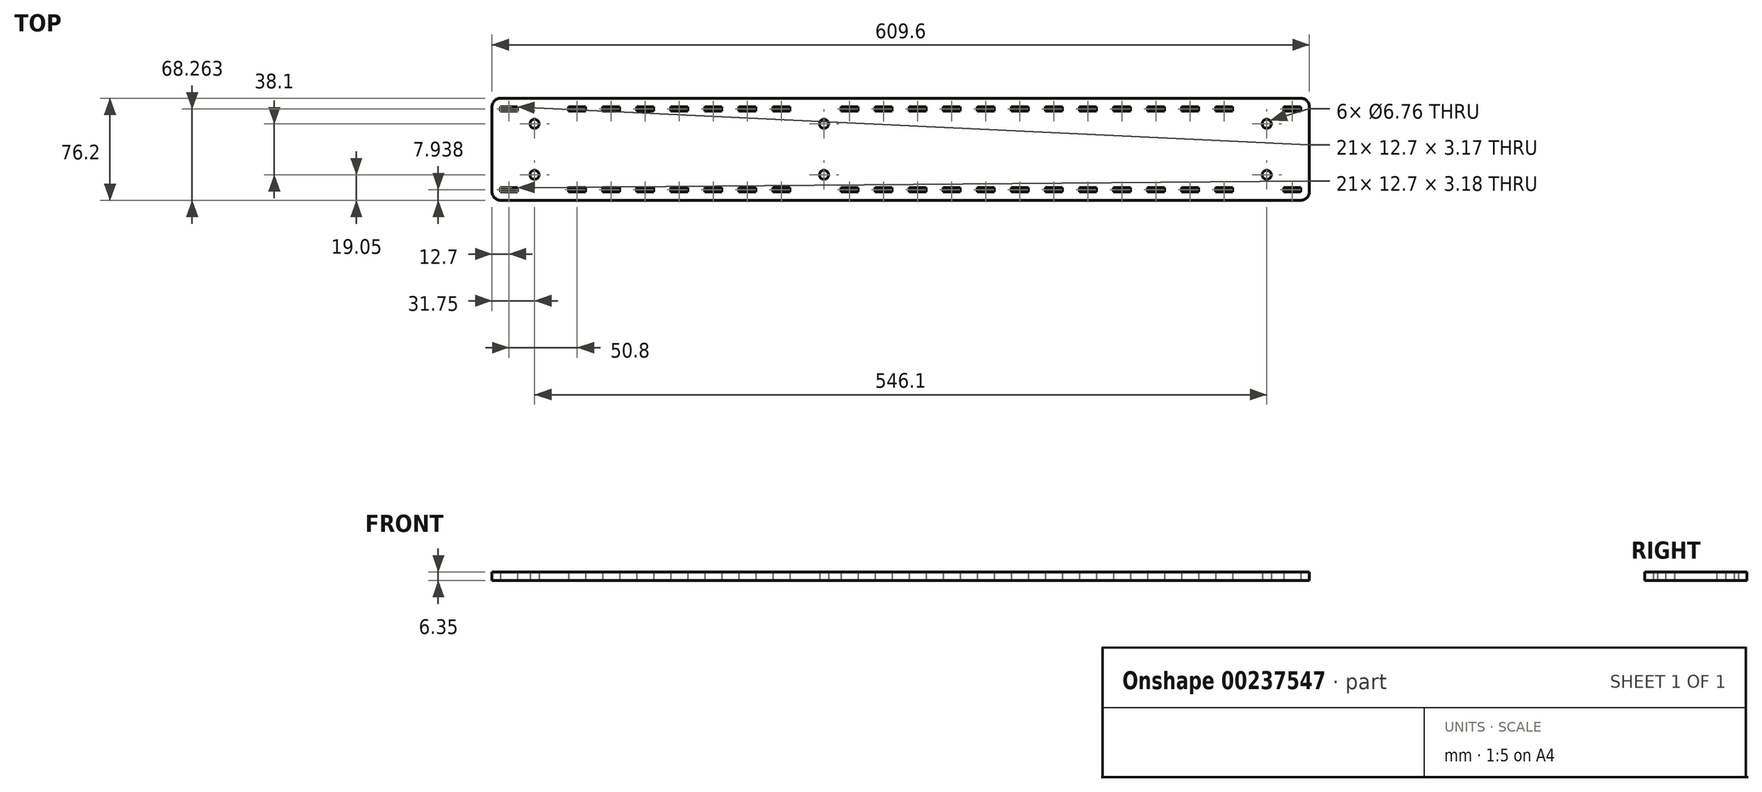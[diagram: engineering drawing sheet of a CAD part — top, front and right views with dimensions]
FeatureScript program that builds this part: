
annotation { "Feature Type Name" : "Feature", "Feature Type Description" : "" }
export const myFeature = defineFeature(function(context is Context, id is Id, definition is map)
    precondition{}
    {
        {
            var Q0;
            Q0=qCreatedBy(makeId("Top.planeOp"),FACE);
            var sketch = newSketch(context, id + "F0", { "sketchPlane" : qUnion([Q0])});
            skLineSegment(sketch, "E0.bottom", {"start": v(0, 0) * mm, "end": v(609.6, 0) * mm});
            skLineSegment(sketch, "E0.top", {"start": v(0, 76.2) * mm, "end": v(609.6, 76.2) * mm});
            skLineSegment(sketch, "E0.left", {"start": v(0, 0) * mm, "end": v(0, 76.2) * mm});
            skLineSegment(sketch, "E0.right", {"start": v(609.6, 0) * mm, "end": v(609.6, 76.2) * mm});
            skLineSegment(sketch, "E1", {"start": v(0, 76.2) * mm, "end": v(0, 69.85) * mm});
            skLineSegment(sketch, "E2", {"start": v(6.35, 69.85) * mm, "end": v(6.35, 66.68) * mm});
            skLineSegment(sketch, "E3", {"start": v(6.35, 66.68) * mm, "end": v(19.05, 66.68) * mm});
            skLineSegment(sketch, "E4", {"start": v(19.05, 66.68) * mm, "end": v(19.05, 69.85) * mm});
            skLineSegment(sketch, "E5", {"start": v(19.05, 69.85) * mm, "end": v(6.35, 69.85) * mm});
            skLineSegment(sketch, "E6.2.0.0", {"start": v(57.15, 66.68) * mm, "end": v(69.85, 66.68) * mm});
            skLineSegment(sketch, "E6.2.0.1", {"start": v(69.85, 69.85) * mm, "end": v(57.15, 69.85) * mm});
            skLineSegment(sketch, "E6.2.0.2", {"start": v(57.15, 69.85) * mm, "end": v(57.15, 66.68) * mm});
            skLineSegment(sketch, "E6.2.0.3", {"start": v(69.85, 66.67) * mm, "end": v(69.85, 69.85) * mm});
            skLineSegment(sketch, "E6.3.0.0", {"start": v(82.55, 66.68) * mm, "end": v(95.25, 66.68) * mm});
            skLineSegment(sketch, "E6.3.0.1", {"start": v(95.25, 69.85) * mm, "end": v(82.55, 69.85) * mm});
            skLineSegment(sketch, "E6.3.0.2", {"start": v(82.55, 69.85) * mm, "end": v(82.55, 66.68) * mm});
            skLineSegment(sketch, "E6.3.0.3", {"start": v(95.25, 66.67) * mm, "end": v(95.25, 69.85) * mm});
            skLineSegment(sketch, "E6.4.0.0", {"start": v(107.95, 66.68) * mm, "end": v(120.65, 66.68) * mm});
            skLineSegment(sketch, "E6.4.0.1", {"start": v(120.65, 69.85) * mm, "end": v(107.95, 69.85) * mm});
            skLineSegment(sketch, "E6.4.0.2", {"start": v(107.95, 69.85) * mm, "end": v(107.95, 66.68) * mm});
            skLineSegment(sketch, "E6.4.0.3", {"start": v(120.65, 66.67) * mm, "end": v(120.65, 69.85) * mm});
            skLineSegment(sketch, "E6.5.0.0", {"start": v(133.35, 66.68) * mm, "end": v(146.05, 66.68) * mm});
            skLineSegment(sketch, "E6.5.0.1", {"start": v(146.05, 69.85) * mm, "end": v(133.35, 69.85) * mm});
            skLineSegment(sketch, "E6.5.0.2", {"start": v(133.35, 69.85) * mm, "end": v(133.35, 66.68) * mm});
            skLineSegment(sketch, "E6.5.0.3", {"start": v(146.05, 66.67) * mm, "end": v(146.05, 69.85) * mm});
            skLineSegment(sketch, "E6.6.0.0", {"start": v(158.75, 66.68) * mm, "end": v(171.45, 66.68) * mm});
            skLineSegment(sketch, "E6.6.0.1", {"start": v(171.45, 69.85) * mm, "end": v(158.75, 69.85) * mm});
            skLineSegment(sketch, "E6.6.0.2", {"start": v(158.75, 69.85) * mm, "end": v(158.75, 66.68) * mm});
            skLineSegment(sketch, "E6.6.0.3", {"start": v(171.45, 66.67) * mm, "end": v(171.45, 69.85) * mm});
            skLineSegment(sketch, "E6.7.0.0", {"start": v(184.15, 66.68) * mm, "end": v(196.85, 66.68) * mm});
            skLineSegment(sketch, "E6.7.0.1", {"start": v(196.85, 69.85) * mm, "end": v(184.15, 69.85) * mm});
            skLineSegment(sketch, "E6.7.0.2", {"start": v(184.15, 69.85) * mm, "end": v(184.15, 66.68) * mm});
            skLineSegment(sketch, "E6.7.0.3", {"start": v(196.85, 66.67) * mm, "end": v(196.85, 69.85) * mm});
            skLineSegment(sketch, "E6.8.0.0", {"start": v(209.55, 66.68) * mm, "end": v(222.25, 66.68) * mm});
            skLineSegment(sketch, "E6.8.0.1", {"start": v(222.25, 69.85) * mm, "end": v(209.55, 69.85) * mm});
            skLineSegment(sketch, "E6.8.0.2", {"start": v(209.55, 69.85) * mm, "end": v(209.55, 66.68) * mm});
            skLineSegment(sketch, "E6.8.0.3", {"start": v(222.25, 66.67) * mm, "end": v(222.25, 69.85) * mm});
            skLineSegment(sketch, "E6.10.0.0", {"start": v(260.35, 66.68) * mm, "end": v(273.05, 66.68) * mm});
            skLineSegment(sketch, "E6.10.0.1", {"start": v(273.05, 69.85) * mm, "end": v(260.35, 69.85) * mm});
            skLineSegment(sketch, "E6.10.0.2", {"start": v(260.35, 69.85) * mm, "end": v(260.35, 66.68) * mm});
            skLineSegment(sketch, "E6.10.0.3", {"start": v(273.05, 66.67) * mm, "end": v(273.05, 69.85) * mm});
            skLineSegment(sketch, "E6.11.0.0", {"start": v(285.75, 66.68) * mm, "end": v(298.45, 66.68) * mm});
            skLineSegment(sketch, "E6.11.0.1", {"start": v(298.45, 69.85) * mm, "end": v(285.75, 69.85) * mm});
            skLineSegment(sketch, "E6.11.0.2", {"start": v(285.75, 69.85) * mm, "end": v(285.75, 66.68) * mm});
            skLineSegment(sketch, "E6.11.0.3", {"start": v(298.45, 66.67) * mm, "end": v(298.45, 69.85) * mm});
            skLineSegment(sketch, "E6.12.0.0", {"start": v(311.15, 66.68) * mm, "end": v(323.85, 66.68) * mm});
            skLineSegment(sketch, "E6.12.0.1", {"start": v(323.85, 69.85) * mm, "end": v(311.15, 69.85) * mm});
            skLineSegment(sketch, "E6.12.0.2", {"start": v(311.15, 69.85) * mm, "end": v(311.15, 66.68) * mm});
            skLineSegment(sketch, "E6.12.0.3", {"start": v(323.85, 66.67) * mm, "end": v(323.85, 69.85) * mm});
            skLineSegment(sketch, "E6.13.0.0", {"start": v(336.55, 66.68) * mm, "end": v(349.25, 66.68) * mm});
            skLineSegment(sketch, "E6.13.0.1", {"start": v(349.25, 69.85) * mm, "end": v(336.55, 69.85) * mm});
            skLineSegment(sketch, "E6.13.0.2", {"start": v(336.55, 69.85) * mm, "end": v(336.55, 66.68) * mm});
            skLineSegment(sketch, "E6.13.0.3", {"start": v(349.25, 66.67) * mm, "end": v(349.25, 69.85) * mm});
            skLineSegment(sketch, "E6.14.0.0", {"start": v(361.95, 66.68) * mm, "end": v(374.65, 66.68) * mm});
            skLineSegment(sketch, "E6.14.0.1", {"start": v(374.65, 69.85) * mm, "end": v(361.95, 69.85) * mm});
            skLineSegment(sketch, "E6.14.0.2", {"start": v(361.95, 69.85) * mm, "end": v(361.95, 66.68) * mm});
            skLineSegment(sketch, "E6.14.0.3", {"start": v(374.65, 66.67) * mm, "end": v(374.65, 69.85) * mm});
            skLineSegment(sketch, "E6.15.0.0", {"start": v(387.35, 66.68) * mm, "end": v(400.05, 66.68) * mm});
            skLineSegment(sketch, "E6.15.0.1", {"start": v(400.05, 69.85) * mm, "end": v(387.35, 69.85) * mm});
            skLineSegment(sketch, "E6.15.0.2", {"start": v(387.35, 69.85) * mm, "end": v(387.35, 66.68) * mm});
            skLineSegment(sketch, "E6.15.0.3", {"start": v(400.05, 66.67) * mm, "end": v(400.05, 69.85) * mm});
            skLineSegment(sketch, "E6.16.0.0", {"start": v(412.75, 66.68) * mm, "end": v(425.45, 66.68) * mm});
            skLineSegment(sketch, "E6.16.0.1", {"start": v(425.45, 69.85) * mm, "end": v(412.75, 69.85) * mm});
            skLineSegment(sketch, "E6.16.0.2", {"start": v(412.75, 69.85) * mm, "end": v(412.75, 66.68) * mm});
            skLineSegment(sketch, "E6.16.0.3", {"start": v(425.45, 66.67) * mm, "end": v(425.45, 69.85) * mm});
            skLineSegment(sketch, "E6.17.0.0", {"start": v(438.15, 66.68) * mm, "end": v(450.85, 66.68) * mm});
            skLineSegment(sketch, "E6.17.0.1", {"start": v(450.85, 69.85) * mm, "end": v(438.15, 69.85) * mm});
            skLineSegment(sketch, "E6.17.0.2", {"start": v(438.15, 69.85) * mm, "end": v(438.15, 66.68) * mm});
            skLineSegment(sketch, "E6.17.0.3", {"start": v(450.85, 66.67) * mm, "end": v(450.85, 69.85) * mm});
            skLineSegment(sketch, "E6.18.0.0", {"start": v(463.55, 66.68) * mm, "end": v(476.25, 66.68) * mm});
            skLineSegment(sketch, "E6.18.0.1", {"start": v(476.25, 69.85) * mm, "end": v(463.55, 69.85) * mm});
            skLineSegment(sketch, "E6.18.0.2", {"start": v(463.55, 69.85) * mm, "end": v(463.55, 66.68) * mm});
            skLineSegment(sketch, "E6.18.0.3", {"start": v(476.25, 66.67) * mm, "end": v(476.25, 69.85) * mm});
            skLineSegment(sketch, "E7.0.19.0", {"start": v(488.95, 66.67) * mm, "end": v(501.65, 66.67) * mm});
            skLineSegment(sketch, "E7.3.19.0", {"start": v(501.65, 69.85) * mm, "end": v(488.95, 69.85) * mm});
            skLineSegment(sketch, "E7.6.19.0", {"start": v(488.95, 69.85) * mm, "end": v(488.95, 66.68) * mm});
            skLineSegment(sketch, "E7.9.19.0", {"start": v(501.65, 66.67) * mm, "end": v(501.65, 69.85) * mm});
            skLineSegment(sketch, "E7.0.20.0", {"start": v(514.35, 66.67) * mm, "end": v(527.05, 66.67) * mm});
            skLineSegment(sketch, "E7.3.20.0", {"start": v(527.05, 69.85) * mm, "end": v(514.35, 69.85) * mm});
            skLineSegment(sketch, "E7.6.20.0", {"start": v(514.35, 69.85) * mm, "end": v(514.35, 66.68) * mm});
            skLineSegment(sketch, "E7.9.20.0", {"start": v(527.05, 66.67) * mm, "end": v(527.05, 69.85) * mm});
            skLineSegment(sketch, "E7.0.21.0", {"start": v(539.75, 66.67) * mm, "end": v(552.45, 66.67) * mm});
            skLineSegment(sketch, "E7.3.21.0", {"start": v(552.45, 69.85) * mm, "end": v(539.75, 69.85) * mm});
            skLineSegment(sketch, "E7.6.21.0", {"start": v(539.75, 69.85) * mm, "end": v(539.75, 66.68) * mm});
            skLineSegment(sketch, "E7.9.21.0", {"start": v(552.45, 66.67) * mm, "end": v(552.45, 69.85) * mm});
            skLineSegment(sketch, "E8.0.23.0", {"start": v(590.55, 66.67) * mm, "end": v(603.25, 66.67) * mm});
            skLineSegment(sketch, "E8.3.23.0", {"start": v(603.25, 69.85) * mm, "end": v(590.55, 69.85) * mm});
            skLineSegment(sketch, "E8.6.23.0", {"start": v(590.55, 69.85) * mm, "end": v(590.55, 66.68) * mm});
            skLineSegment(sketch, "E8.9.23.0", {"start": v(603.25, 66.67) * mm, "end": v(603.25, 69.85) * mm});
            skLineSegment(sketch, "E9.MirrorCS", {"start": v(387.35, 6.35) * mm, "end": v(387.35, 9.52) * mm});
            skLineSegment(sketch, "E10.MirrorCS", {"start": v(539.75, 6.35) * mm, "end": v(539.75, 9.52) * mm});
            skLineSegment(sketch, "E11.MirrorCS", {"start": v(336.55, 6.35) * mm, "end": v(336.55, 9.52) * mm});
            skLineSegment(sketch, "E12.MirrorCS", {"start": v(438.15, 6.35) * mm, "end": v(438.15, 9.52) * mm});
            skLineSegment(sketch, "E13.MirrorCS", {"start": v(488.95, 6.35) * mm, "end": v(488.95, 9.52) * mm});
            skLineSegment(sketch, "E14.MirrorCS", {"start": v(590.55, 6.35) * mm, "end": v(590.55, 9.52) * mm});
            skLineSegment(sketch, "E15.MirrorCS", {"start": v(552.45, 9.53) * mm, "end": v(552.45, 6.35) * mm});
            skLineSegment(sketch, "E16.MirrorCS", {"start": v(501.65, 9.53) * mm, "end": v(501.65, 6.35) * mm});
            skLineSegment(sketch, "E17.MirrorCS", {"start": v(603.25, 9.53) * mm, "end": v(603.25, 6.35) * mm});
            skLineSegment(sketch, "E18.MirrorCS", {"start": v(463.55, 6.35) * mm, "end": v(463.55, 9.52) * mm});
            skLineSegment(sketch, "E19.MirrorCS", {"start": v(361.95, 6.35) * mm, "end": v(361.95, 9.52) * mm});
            skLineSegment(sketch, "E20.MirrorCS", {"start": v(311.15, 6.35) * mm, "end": v(311.15, 9.52) * mm});
            skLineSegment(sketch, "E21.MirrorCS", {"start": v(412.75, 6.35) * mm, "end": v(412.75, 9.52) * mm});
            skLineSegment(sketch, "E22.MirrorCS", {"start": v(374.65, 9.53) * mm, "end": v(374.65, 6.35) * mm});
            skLineSegment(sketch, "E23.MirrorCS", {"start": v(425.45, 9.53) * mm, "end": v(425.45, 6.35) * mm});
            skLineSegment(sketch, "E24.MirrorCS", {"start": v(323.85, 9.53) * mm, "end": v(323.85, 6.35) * mm});
            skLineSegment(sketch, "E25.MirrorCS", {"start": v(476.25, 9.53) * mm, "end": v(476.25, 6.35) * mm});
            skLineSegment(sketch, "E26.MirrorCS", {"start": v(527.05, 9.53) * mm, "end": v(527.05, 6.35) * mm});
            skLineSegment(sketch, "E27.MirrorCS", {"start": v(450.85, 9.53) * mm, "end": v(450.85, 6.35) * mm});
            skLineSegment(sketch, "E28.MirrorCS", {"start": v(349.25, 9.53) * mm, "end": v(349.25, 6.35) * mm});
            skLineSegment(sketch, "E29.MirrorCS", {"start": v(400.05, 9.53) * mm, "end": v(400.05, 6.35) * mm});
            skLineSegment(sketch, "E30.MirrorCS", {"start": v(514.35, 6.35) * mm, "end": v(514.35, 9.52) * mm});
            skLineSegment(sketch, "E31.MirrorCS", {"start": v(387.35, 9.52) * mm, "end": v(400.05, 9.52) * mm});
            skLineSegment(sketch, "E32.MirrorCS", {"start": v(336.55, 9.52) * mm, "end": v(349.25, 9.52) * mm});
            skLineSegment(sketch, "E33.MirrorCS", {"start": v(438.15, 9.52) * mm, "end": v(450.85, 9.52) * mm});
            skLineSegment(sketch, "E34.MirrorCS", {"start": v(488.95, 9.53) * mm, "end": v(501.65, 9.53) * mm});
            skLineSegment(sketch, "E35.MirrorCS", {"start": v(400.05, 6.35) * mm, "end": v(387.35, 6.35) * mm});
            skLineSegment(sketch, "E36.MirrorCS", {"start": v(590.55, 9.53) * mm, "end": v(603.25, 9.53) * mm});
            skLineSegment(sketch, "E37.MirrorCS", {"start": v(349.25, 6.35) * mm, "end": v(336.55, 6.35) * mm});
            skLineSegment(sketch, "E38.MirrorCS", {"start": v(539.75, 9.53) * mm, "end": v(552.45, 9.53) * mm});
            skLineSegment(sketch, "E39.MirrorCS", {"start": v(450.85, 6.35) * mm, "end": v(438.15, 6.35) * mm});
            skLineSegment(sketch, "E40.MirrorCS", {"start": v(501.65, 6.35) * mm, "end": v(488.95, 6.35) * mm});
            skLineSegment(sketch, "E41.MirrorCS", {"start": v(603.25, 6.35) * mm, "end": v(590.55, 6.35) * mm});
            skLineSegment(sketch, "E42.MirrorCS", {"start": v(552.45, 6.35) * mm, "end": v(539.75, 6.35) * mm});
            skLineSegment(sketch, "E43.MirrorCS", {"start": v(463.55, 9.52) * mm, "end": v(476.25, 9.52) * mm});
            skLineSegment(sketch, "E44.MirrorCS", {"start": v(361.95, 9.52) * mm, "end": v(374.65, 9.52) * mm});
            skLineSegment(sketch, "E45.MirrorCS", {"start": v(476.25, 6.35) * mm, "end": v(463.55, 6.35) * mm});
            skLineSegment(sketch, "E46.MirrorCS", {"start": v(374.65, 6.35) * mm, "end": v(361.95, 6.35) * mm});
            skLineSegment(sketch, "E47.MirrorCS", {"start": v(412.75, 9.52) * mm, "end": v(425.45, 9.52) * mm});
            skLineSegment(sketch, "E48.MirrorCS", {"start": v(311.15, 9.52) * mm, "end": v(323.85, 9.52) * mm});
            skLineSegment(sketch, "E49.MirrorCS", {"start": v(323.85, 6.35) * mm, "end": v(311.15, 6.35) * mm});
            skLineSegment(sketch, "E50.MirrorCS", {"start": v(514.35, 9.53) * mm, "end": v(527.05, 9.53) * mm});
            skLineSegment(sketch, "E51.MirrorCS", {"start": v(425.45, 6.35) * mm, "end": v(412.75, 6.35) * mm});
            skLineSegment(sketch, "E52.MirrorCS", {"start": v(527.05, 6.35) * mm, "end": v(514.35, 6.35) * mm});
            skLineSegment(sketch, "E53.MirrorCS", {"start": v(285.75, 9.52) * mm, "end": v(298.45, 9.52) * mm});
            skLineSegment(sketch, "E54.MirrorCS", {"start": v(273.05, 9.53) * mm, "end": v(273.05, 6.35) * mm});
            skLineSegment(sketch, "E55.MirrorCS", {"start": v(260.35, 6.35) * mm, "end": v(260.35, 9.52) * mm});
            skLineSegment(sketch, "E56.MirrorCS", {"start": v(273.05, 6.35) * mm, "end": v(260.35, 6.35) * mm});
            skLineSegment(sketch, "E57.MirrorCS", {"start": v(260.35, 9.52) * mm, "end": v(273.05, 9.52) * mm});
            skLineSegment(sketch, "E58.MirrorCS", {"start": v(222.25, 9.53) * mm, "end": v(222.25, 6.35) * mm});
            skLineSegment(sketch, "E59.MirrorCS", {"start": v(222.25, 6.35) * mm, "end": v(209.55, 6.35) * mm});
            skLineSegment(sketch, "E60.MirrorCS", {"start": v(209.55, 9.52) * mm, "end": v(222.25, 9.52) * mm});
            skLineSegment(sketch, "E61.MirrorCS", {"start": v(298.45, 9.53) * mm, "end": v(298.45, 6.35) * mm});
            skLineSegment(sketch, "E62.MirrorCS", {"start": v(285.75, 6.35) * mm, "end": v(285.75, 9.52) * mm});
            skLineSegment(sketch, "E63.MirrorCS", {"start": v(298.45, 6.35) * mm, "end": v(285.75, 6.35) * mm});
            skLineSegment(sketch, "E64.MirrorCS", {"start": v(6.35, 6.35) * mm, "end": v(6.35, 9.52) * mm});
            skLineSegment(sketch, "E65.MirrorCS", {"start": v(19.05, 9.53) * mm, "end": v(19.05, 6.35) * mm});
            skLineSegment(sketch, "E66.MirrorCS", {"start": v(171.45, 9.53) * mm, "end": v(171.45, 6.35) * mm});
            skLineSegment(sketch, "E67.MirrorCS", {"start": v(69.85, 9.53) * mm, "end": v(69.85, 6.35) * mm});
            skLineSegment(sketch, "E68.MirrorCS", {"start": v(82.55, 6.35) * mm, "end": v(82.55, 9.52) * mm});
            skLineSegment(sketch, "E69.MirrorCS", {"start": v(184.15, 6.35) * mm, "end": v(184.15, 9.52) * mm});
            skLineSegment(sketch, "E70.MirrorCS", {"start": v(95.25, 9.53) * mm, "end": v(95.25, 6.35) * mm});
            skLineSegment(sketch, "E71.MirrorCS", {"start": v(196.85, 9.53) * mm, "end": v(196.85, 6.35) * mm});
            skLineSegment(sketch, "E72.MirrorCS", {"start": v(146.05, 9.53) * mm, "end": v(146.05, 6.35) * mm});
            skLineSegment(sketch, "E73.MirrorCS", {"start": v(107.95, 6.35) * mm, "end": v(107.95, 9.52) * mm});
            skLineSegment(sketch, "E74.MirrorCS", {"start": v(133.35, 6.35) * mm, "end": v(133.35, 9.52) * mm});
            skLineSegment(sketch, "E75.MirrorCS", {"start": v(120.65, 9.53) * mm, "end": v(120.65, 6.35) * mm});
            skLineSegment(sketch, "E76.MirrorCS", {"start": v(6.35, 9.53) * mm, "end": v(19.05, 9.53) * mm});
            skLineSegment(sketch, "E77.MirrorCS", {"start": v(19.05, 6.35) * mm, "end": v(6.35, 6.35) * mm});
            skLineSegment(sketch, "E78.MirrorCS", {"start": v(57.15, 6.35) * mm, "end": v(57.15, 9.52) * mm});
            skLineSegment(sketch, "E79.MirrorCS", {"start": v(158.75, 6.35) * mm, "end": v(158.75, 9.52) * mm});
            skLineSegment(sketch, "E80.MirrorCS", {"start": v(184.15, 9.52) * mm, "end": v(196.85, 9.52) * mm});
            skLineSegment(sketch, "E81.MirrorCS", {"start": v(82.55, 9.52) * mm, "end": v(95.25, 9.52) * mm});
            skLineSegment(sketch, "E82.MirrorCS", {"start": v(95.25, 6.35) * mm, "end": v(82.55, 6.35) * mm});
            skLineSegment(sketch, "E83.MirrorCS", {"start": v(196.85, 6.35) * mm, "end": v(184.15, 6.35) * mm});
            skLineSegment(sketch, "E84.MirrorCS", {"start": v(107.95, 9.52) * mm, "end": v(120.65, 9.52) * mm});
            skLineSegment(sketch, "E85.MirrorCS", {"start": v(120.65, 6.35) * mm, "end": v(107.95, 6.35) * mm});
            skLineSegment(sketch, "E86.MirrorCS", {"start": v(146.05, 6.35) * mm, "end": v(133.35, 6.35) * mm});
            skLineSegment(sketch, "E87.MirrorCS", {"start": v(158.75, 9.52) * mm, "end": v(171.45, 9.52) * mm});
            skLineSegment(sketch, "E88.MirrorCS", {"start": v(133.35, 9.52) * mm, "end": v(146.05, 9.52) * mm});
            skLineSegment(sketch, "E89.MirrorCS", {"start": v(171.45, 6.35) * mm, "end": v(158.75, 6.35) * mm});
            skLineSegment(sketch, "E90.MirrorCS", {"start": v(57.15, 9.52) * mm, "end": v(69.85, 9.52) * mm});
            skLineSegment(sketch, "E91.MirrorCS", {"start": v(69.85, 6.35) * mm, "end": v(57.15, 6.35) * mm});
            skCircle(sketch, "E92", {"center": v(31.75, 57.15) * mm, "radius": 3.38 * mm});
            skCircle(sketch, "E93", {"center": v(247.65, 57.15) * mm, "radius": 3.38 * mm});
            skCircle(sketch, "E94", {"center": v(577.85, 57.15) * mm, "radius": 3.38 * mm});
            skCircle(sketch, "E95.MirrorC", {"center": v(31.75, 19.05) * mm, "radius": 3.38 * mm});
            skCircle(sketch, "E96.MirrorC", {"center": v(247.65, 19.05) * mm, "radius": 3.38 * mm});
            skCircle(sketch, "E97.MirrorC", {"center": v(577.85, 19.05) * mm, "radius": 3.38 * mm});
            skLineSegment(sketch, "E98", {"start": v(209.55, 6.35) * mm, "end": v(209.55, 9.52) * mm});
            skSolve(sketch);
        }
        {
            var Q0;
            Q0 = qSketchRegion(id + "F0", true);
            extrude(context, id + "F1", {"entities" : qUnion([Q0]), "depth" : 6.35 * mm});
        }
        {
            var Q0;
            Q0=makeQuery(id+"F1.opExtrude","SWEPT_EDGE",EDGE,{"disambiguationData":[OSD([sQuery(id+"F0.wireOp",EDGE,"E0.top"),sQuery(id+"F0.wireOp",EDGE,"E0.right")])]});
            var Q1;
            Q1=makeQuery(id+"F1.opExtrude","SWEPT_EDGE",EDGE,{"disambiguationData":[OSD([sQuery(id+"F0.wireOp",EDGE,"E0.bottom"),sQuery(id+"F0.wireOp",EDGE,"E0.right")])]});
            var Q2;
            Q2=makeQuery(id+"F1.opExtrude","SWEPT_EDGE",EDGE,{"disambiguationData":[OSD([sQuery(id+"F0.wireOp",EDGE,"E0.top"),sQuery(id+"F0.wireOp",EDGE,"E1")])]});
            var Q3;
            Q3=makeQuery(id+"F1.opExtrude","SWEPT_EDGE",EDGE,{"disambiguationData":[OSD([sQuery(id+"F0.wireOp",EDGE,"E0.bottom"),sQuery(id+"F0.wireOp",EDGE,"E0.left")])]});
            fillet(context, id + "F2", {"entities" : qUnion([Q0, Q1, Q2, Q3]), "radius" : 6.35 * mm, "tangentPropagation" : true, "allowEdgeOverflow" : false});
        }
    });
